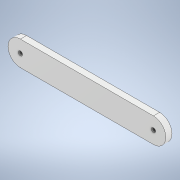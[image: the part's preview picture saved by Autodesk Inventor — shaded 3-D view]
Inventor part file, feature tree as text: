
AUTODESK INVENTOR PART (.ipt)
format: ipt  version: 2021 (Build 250183000, 183)  size: 103,936 bytes
history: native  units: in
note: dims shown in document units (in); Inventor stores cm internally (conversion verified against a paired STEP export)
features: extrude x1, sketch x1
ambient origin geometry x8: Origin, YZ Plane, XZ Plane, XY Plane, X Axis, Y Axis, Z Axis, Center Point
bodies: Solid1 (feature_tree)
feature tree (2):
  extrude  "Extrusion1"  Depth=1.5748in
  sketch  "Sketch1"  dims[d0=8.4646in d1=1.5748in d4=0.2756in d5=0.2756in d6=0.3937in d7=0.0in]
